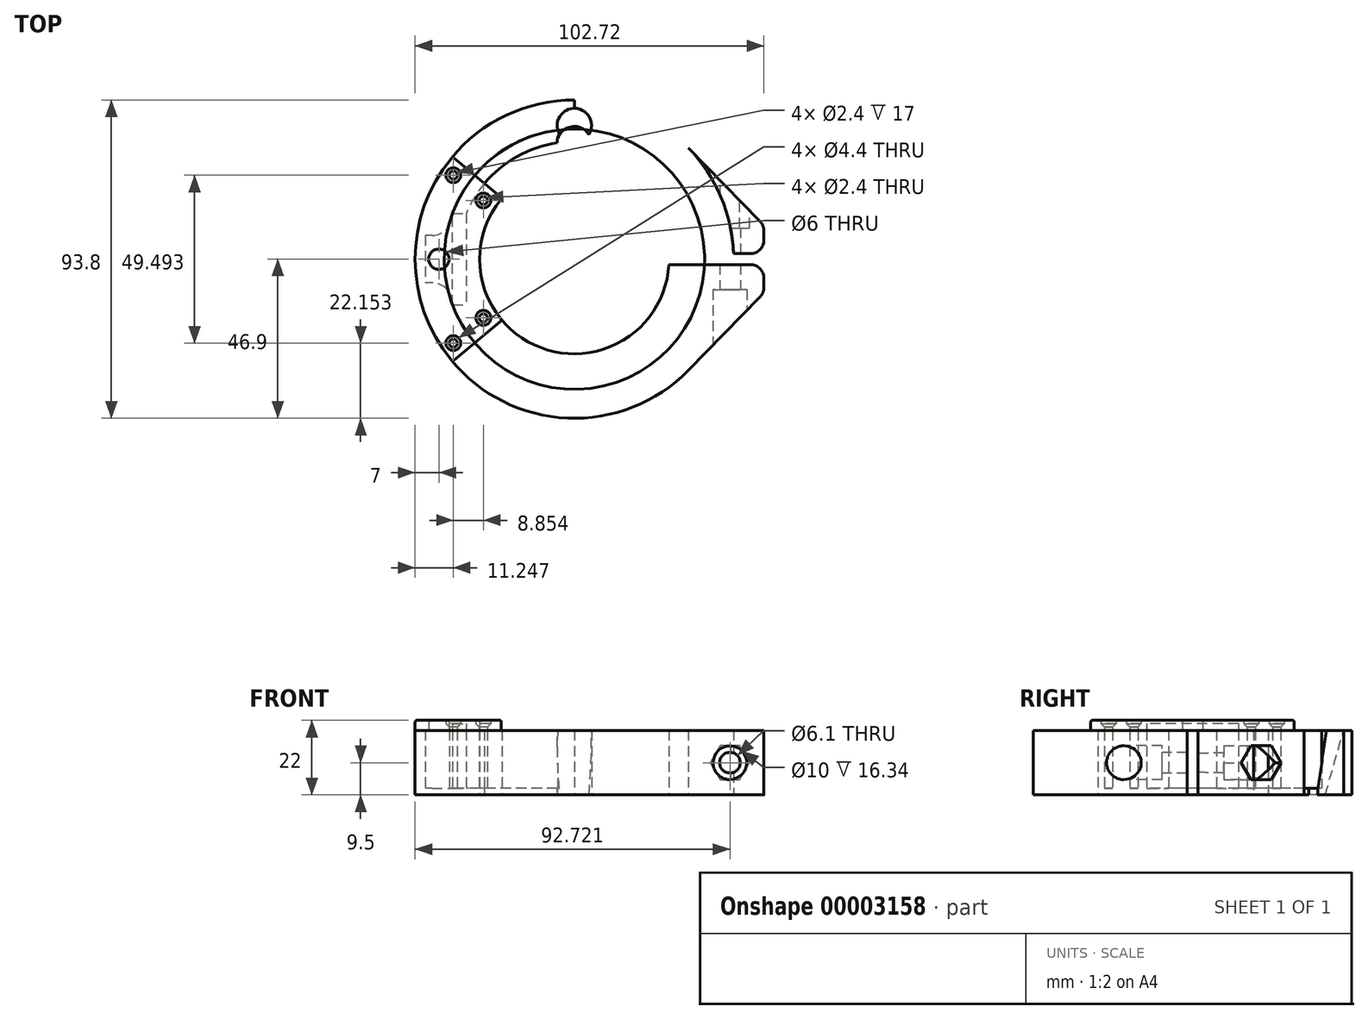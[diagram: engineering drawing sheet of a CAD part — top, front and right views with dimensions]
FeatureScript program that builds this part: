
annotation { "Feature Type Name" : "Feature", "Feature Type Description" : "" }
export const myFeature = defineFeature(function(context is Context, id is Id, definition is map)
    precondition{}
    {
        {
            var Q0;
            Q0=qCreatedBy(makeId("Top.planeOp"),FACE);
            var sketch = newSketch(context, id + "F0", { "sketchPlane" : qUnion([Q0])});
            skCircle(sketch, "E0", {"center": v(0, 0) * mm, "radius": 31.9 * mm, "construction": true});
            skCircle(sketch, "E1", {"center": v(0, 0) * mm, "radius": 43.4 * mm, "construction": true});
            skLineSegment(sketch, "E2", {"start": v(55.82, 1.6) * mm, "end": v(0, 1.6) * mm});
            skLineSegment(sketch, "E3", {"start": v(0, 1.6) * mm, "end": v(0, -1.6) * mm});
            skLineSegment(sketch, "E4", {"start": v(0, -1.6) * mm, "end": v(55.82, -1.6) * mm});
            skLineSegment(sketch, "E5", {"start": v(45.82, 10) * mm, "end": v(55.82, 10) * mm});
            skLineSegment(sketch, "E6", {"start": v(55.82, 10) * mm, "end": v(55.82, -10) * mm});
            skLineSegment(sketch, "E7", {"start": v(55.82, -10) * mm, "end": v(45.82, -10) * mm});
            skLineSegment(sketch, "E8", {"start": v(-31.9, 13.5) * mm, "end": v(-31.9, -13.5) * mm});
            skLineSegment(sketch, "E9", {"start": v(-35.9, -13.5) * mm, "end": v(-35.9, 13.5) * mm});
            skCircle(sketch, "E10", {"center": v(-39.9, 0) * mm, "radius": 3 * mm});
            skLineSegment(sketch, "E11", {"start": v(-35.9, 0) * mm, "end": v(-31.9, 0) * mm, "construction": true});
            skCircle(sketch, "E12", {"center": v(0, 0) * mm, "radius": 46.9 * mm});
            skLineSegment(sketch, "E13", {"start": v(-35.9, -13.5) * mm, "end": v(-31.9, -13.5) * mm});
            skLineSegment(sketch, "E14", {"start": v(-35.9, 13.5) * mm, "end": v(-31.9, 13.5) * mm});
            skLineSegment(sketch, "E15.rect.bottom", {"start": v(-35.9, 7) * mm, "end": v(-43.9, 7) * mm});
            skLineSegment(sketch, "E15.rect.top", {"start": v(-35.9, -7) * mm, "end": v(-43.9, -7) * mm});
            skLineSegment(sketch, "E15.rect.left", {"start": v(-35.9, 7) * mm, "end": v(-35.9, -7) * mm});
            skLineSegment(sketch, "E15.rect.right", {"start": v(-43.9, 7) * mm, "end": v(-43.9, -7) * mm});
            skCircle(sketch, "E16", {"center": v(0, 39.4) * mm, "radius": 5.05 * mm});
            skLineSegment(sketch, "E17", {"start": v(0, 31.9) * mm, "end": v(0, 46.9) * mm});
            skCircle(sketch, "E18", {"center": v(0, 0) * mm, "radius": 27.9 * mm});
            skLineSegment(sketch, "E19", {"start": v(-31.9, 0) * mm, "end": v(-27.9, 0) * mm});
            skLineSegment(sketch, "E20", {"start": v(0, 0) * mm, "end": v(55.82, 0) * mm, "construction": true});
            skArc(sketch, "E21", {"start": v(-4.87, 38.04) * mm, "mid": v(-23.8, 30.08) * mm, "end": v(-35.9, 13.5) * mm});
            skLineSegment(sketch, "E22", {"start": v(-21.36, 17.95) * mm, "end": v(-35.9, 30.18) * mm});
            skLineSegment(sketch, "E23", {"start": v(-35.9, -30.18) * mm, "end": v(-21.36, -17.95) * mm});
            skLineSegment(sketch, "E24", {"start": v(-35.9, 30.18) * mm, "end": v(-35.9, -30.18) * mm, "construction": true});
            skArc(sketch, "E25.trimOffspring", {"start": v(-1.6, 34.6) * mm, "mid": v(-19.8, 28.43) * mm, "end": v(-31.9, 13.5) * mm});
            skLineSegment(sketch, "E26.0", {"start": v(-38.34, -27) * mm, "end": v(-23.7, -14.7) * mm, "construction": true});
            skLineSegment(sketch, "E27.0", {"start": v(-23.7, 14.7) * mm, "end": v(-38.34, 27) * mm, "construction": true});
            skCircle(sketch, "E28", {"center": v(-26.8, 17.3) * mm, "radius": 1.2 * mm});
            skCircle(sketch, "E29", {"center": v(-35.65, 24.75) * mm, "radius": 1.2 * mm});
            skCircle(sketch, "E30", {"center": v(-35.65, -24.75) * mm, "radius": 1.2 * mm});
            skCircle(sketch, "E31", {"center": v(-26.8, -17.3) * mm, "radius": 1.2 * mm});
            skLineSegment(sketch, "E32", {"start": v(-43.9, 0) * mm, "end": v(-46.9, 0) * mm, "construction": true});
            skLineSegment(sketch, "E33", {"start": v(0, -43.4) * mm, "end": v(0, -46.9) * mm, "construction": true});
            skLineSegment(sketch, "E34", {"start": v(55.82, 10) * mm, "end": v(33.53, 32.8) * mm});
            skLineSegment(sketch, "E35", {"start": v(55.82, -10) * mm, "end": v(33.53, -32.8) * mm});
            skCircle(sketch, "E36.0", {"center": v(-35.65, 24.75) * mm, "radius": 2.2 * mm});
            skCircle(sketch, "E37.0", {"center": v(-26.8, 17.3) * mm, "radius": 2.2 * mm});
            skCircle(sketch, "E38.0", {"center": v(-35.65, -24.75) * mm, "radius": 2.2 * mm});
            skCircle(sketch, "E39.0", {"center": v(-26.8, -17.3) * mm, "radius": 2.2 * mm});
            skSolve(sketch);
        }
        {
            var Q0;
            {var subQ13=sQuery(id+"F0.wireOp",EDGE,"E13");Q0=makeQuery(id+"F0.imprint","IMPRINT",FACE,{"disambiguationData":[TD([[makeQuery(id+"F0.imprint","IMPRINT",EDGE,{"derivedFrom":subQ13}),-1.0]])]});}
            var Q1;
            {var subQ7=sQuery(id+"F0.wireOp",EDGE,"E19");Q1=makeQuery(id+"F0.imprint","IMPRINT",FACE,{"disambiguationData":[TD([[makeQuery(id+"F0.imprint","IMPRINT",EDGE,{"derivedFrom":subQ7}),1.0]])]});}
            var Q2;
            {var subQ3=sQuery(id+"F0.wireOp",EDGE,"E14");Q2=makeQuery(id+"F0.imprint","IMPRINT",FACE,{"disambiguationData":[TD([[makeQuery(id+"F0.imprint","IMPRINT",EDGE,{"derivedFrom":subQ3}),1.0]])]});}
            var Q3;
            {var subQ2=sQuery(id+"F0.wireOp",EDGE,"E13");Q3=makeQuery(id+"F0.imprint","IMPRINT",FACE,{"disambiguationData":[TD([[makeQuery(id+"F0.imprint","IMPRINT",EDGE,{"derivedFrom":subQ2}),1.0]])]});}
            var Q4;
            Q4=makeQuery(id+"F0.imprint","IMPRINT",FACE,{"disambiguationData":[TD([[makeQuery(id+"F0.imprint","IMPRINT",EDGE,{"derivedFrom":sQuery(id+"F0.wireOp",EDGE,"E10")}),-1.0]])]});
            extrude(context, id + "F1", {"entities" : qUnion([Q0, Q1, Q2, Q3, Q4]), "depth" : 3 * mm});
        }
        {
            var Q0;
            Q0=makeQuery(id+"F0.imprint","IMPRINT",FACE,{"disambiguationData":[TD([[makeQuery(id+"F0.imprint","IMPRINT",EDGE,{"derivedFrom":sQuery(id+"F0.wireOp",EDGE,"E28")}),-1.0]])]});
            var Q1;
            Q1=makeQuery(id+"F0.imprint","IMPRINT",FACE,{"disambiguationData":[TD([[makeQuery(id+"F0.imprint","IMPRINT",EDGE,{"derivedFrom":sQuery(id+"F0.wireOp",EDGE,"E29")}),-1.0]])]});
            var Q2;
            Q2=makeQuery(id+"F0.imprint","IMPRINT",FACE,{"disambiguationData":[TD([[makeQuery(id+"F0.imprint","IMPRINT",EDGE,{"derivedFrom":sQuery(id+"F0.wireOp",EDGE,"E30")}),-1.0]])]});
            var Q3;
            Q3=makeQuery(id+"F0.imprint","IMPRINT",FACE,{"disambiguationData":[TD([[makeQuery(id+"F0.imprint","IMPRINT",EDGE,{"derivedFrom":sQuery(id+"F0.wireOp",EDGE,"E31")}),-1.0]])]});
            extrude(context, id + "F2", {"entities" : qUnion([Q0, Q1, Q2, Q3]), "operationType" : NewBodyOperationType.ADD, "depth" : 2 * mm});
        }
        {
            var Q0;
            {var subQ2=sQuery(id+"F0.wireOp",EDGE,"E13");Q0=makeQuery(id+"F0.imprint","IMPRINT",FACE,{"disambiguationData":[TD([[makeQuery(id+"F0.imprint","IMPRINT",EDGE,{"derivedFrom":subQ2}),1.0]])]});}
            extrude(context, id + "F3", {"entities" : qUnion([Q0]), "operationType" : NewBodyOperationType.REMOVE, "depth" : 2 * mm});
        }
        {
            var Q0;
            Q0=makeQuery(id+"F1.opExtrude","SWEPT_BODY",BODY,{"disambiguationData":[OSD([sQuery(id+"F0.wireOp",EDGE,"E10"),sQuery(id+"F0.wireOp",EDGE,"E12"),sQuery(id+"F0.wireOp",EDGE,"E18"),sQuery(id+"F0.wireOp",EDGE,"E22"),sQuery(id+"F0.wireOp",EDGE,"E23"),sQuery(id+"F0.wireOp",EDGE,"E36.0"),sQuery(id+"F0.wireOp",EDGE,"E37.0"),sQuery(id+"F0.wireOp",EDGE,"E38.0"),sQuery(id+"F0.wireOp",EDGE,"E39.0")])]});
            transform(context, id + "F4", {"entities" : qUnion([Q0]), "transformType" : TransformType.TRANSLATION_3D, "dx" : 0 * mm, "dy" : 0 * mm, "dz" : 19 * mm, "makeCopy" : false});
        }
        {
            var Q0;
            Q0=makeQuery(id+"F2.opExtrude","CAP_EDGE",EDGE,{"disambiguationData":[OSD([sQuery(id+"F0.wireOp",EDGE,"E30")])],"isStart":false});
            var Q1;
            Q1=makeQuery(id+"F2.opExtrude","CAP_EDGE",EDGE,{"disambiguationData":[OSD([sQuery(id+"F0.wireOp",EDGE,"E31")])],"isStart":false});
            var Q2;
            Q2=makeQuery(id+"F2.opExtrude","CAP_EDGE",EDGE,{"disambiguationData":[OSD([sQuery(id+"F0.wireOp",EDGE,"E28")])],"isStart":false});
            var Q3;
            Q3=makeQuery(id+"F2.opExtrude","CAP_EDGE",EDGE,{"disambiguationData":[OSD([sQuery(id+"F0.wireOp",EDGE,"E29")])],"isStart":false});
            chamfer(context, id + "F5", {"entities" : qUnion([Q0, Q1, Q2, Q3]), "width" : 1 * mm, "tangentPropagation" : true});
        }
        {
            var Q0;
            Q0=makeQuery(id+"F1.opExtrude","CAP_EDGE",EDGE,{"disambiguationData":[OSD([sQuery(id+"F0.wireOp",EDGE,"E23")])],"isStart":false});
            var Q1;
            Q1=makeQuery(id+"F1.opExtrude","CAP_EDGE",EDGE,{"disambiguationData":[OSD([sQuery(id+"F0.wireOp",EDGE,"E22")])],"isStart":false});
            var Q2;
            Q2=makeQuery(id+"F1.opExtrude","CAP_EDGE",EDGE,{"disambiguationData":[OSD([sQuery(id+"F0.wireOp",EDGE,"E18")])],"isStart":false});
            var Q3;
            Q3=makeQuery(id+"F1.opExtrude","CAP_EDGE",EDGE,{"disambiguationData":[OSD([sQuery(id+"F0.wireOp",EDGE,"E12")])],"isStart":false});
            var Q4;
            Q4=makeQuery(id+"F1.opExtrude","SWEPT_EDGE",EDGE,{"disambiguationData":[OSD([sQuery(id+"F0.wireOp",EDGE,"E12"),sQuery(id+"F0.wireOp",EDGE,"E23")])]});
            var Q5;
            Q5=makeQuery(id+"F1.opExtrude","SWEPT_EDGE",EDGE,{"disambiguationData":[OSD([sQuery(id+"F0.wireOp",EDGE,"E18"),sQuery(id+"F0.wireOp",EDGE,"E23")])]});
            var Q6;
            Q6=makeQuery(id+"F1.opExtrude","SWEPT_EDGE",EDGE,{"disambiguationData":[OSD([sQuery(id+"F0.wireOp",EDGE,"E12"),sQuery(id+"F0.wireOp",EDGE,"E22")])]});
            var Q7;
            Q7=makeQuery(id+"F1.opExtrude","SWEPT_EDGE",EDGE,{"disambiguationData":[OSD([sQuery(id+"F0.wireOp",EDGE,"E18"),sQuery(id+"F0.wireOp",EDGE,"E22")])]});
            fillet(context, id + "F6", {"entities" : qUnion([Q0, Q1, Q2, Q3, Q4, Q5, Q6, Q7]), "radius" : .5 * mm, "tangentPropagation" : true, "allowEdgeOverflow" : false});
        }
        {
            var Q0;
            {var subQ13=sQuery(id+"F0.wireOp",EDGE,"E13");Q0=makeQuery(id+"F0.imprint","IMPRINT",FACE,{"disambiguationData":[TD([[makeQuery(id+"F0.imprint","IMPRINT",EDGE,{"derivedFrom":subQ13}),-1.0]])]});}
            var Q1;
            {var subQ3=sQuery(id+"F0.wireOp",EDGE,"E5");Q1=makeQuery(id+"F0.imprint","IMPRINT",FACE,{"disambiguationData":[TD([[makeQuery(id+"F0.imprint","IMPRINT",EDGE,{"derivedFrom":subQ3}),-1.0]])]});}
            var Q2;
            {var subQ3=sQuery(id+"F0.wireOp",EDGE,"E7");Q2=makeQuery(id+"F0.imprint","IMPRINT",FACE,{"disambiguationData":[TD([[makeQuery(id+"F0.imprint","IMPRINT",EDGE,{"derivedFrom":subQ3}),-1.0]])]});}
            var Q3;
            {var subQ0=sQuery(id+"F0.wireOp",EDGE,"E23");Q3=makeQuery(id+"F0.imprint","IMPRINT",FACE,{"disambiguationData":[TD([[makeQuery(id+"F0.imprint","IMPRINT",EDGE,{"derivedFrom":subQ0}),-1.0]])]});}
            var Q4;
            {var subQ3=sQuery(id+"F0.wireOp",EDGE,"E12");var subQ7=sQuery(id+"F0.wireOp",EDGE,"E17");var subQ9=makeQuery(id+"F0.imprint","INTERSECT",VERTEX,{"derivedFrom":[subQ3,subQ7]});Q4=makeQuery(id+"F0.imprint","IMPRINT",FACE,{"disambiguationData":[TD([[makeQuery(id+"F0.imprint","IMPRINT",EDGE,{"disambiguationData":[TD([[subQ9,-1.0]])],"derivedFrom":subQ3}),1.0]])]});}
            var Q5;
            {var subQ7=sQuery(id+"F0.wireOp",EDGE,"E19");Q5=makeQuery(id+"F0.imprint","IMPRINT",FACE,{"disambiguationData":[TD([[makeQuery(id+"F0.imprint","IMPRINT",EDGE,{"derivedFrom":subQ7}),1.0]])]});}
            var Q6;
            {var subQ9=sQuery(id+"F0.wireOp",EDGE,"E17");Q6=makeQuery(id+"F0.imprint","IMPRINT",FACE,{"disambiguationData":[TD([[makeQuery(id+"F0.imprint","IMPRINT",EDGE,{"disambiguationData":[TD([[makeQuery(id+"F0.imprint","IMPRINT",VERTEX,{"derivedFrom":sQuery(id+"F0.wireOp",VERTEX,"E17.start")}),-1.0]])],"derivedFrom":subQ9}),1.0]])]});}
            var Q7;
            {var subQ0=sQuery(id+"F0.wireOp",EDGE,"E17");var subQ1=sQuery(id+"F0.wireOp",EDGE,"E16");var subQ3=makeQuery(id+"F0.imprint","INTERSECT",VERTEX,{"disambiguationData":[OD(0.0)],"derivedFrom":[subQ1,subQ0]});Q7=makeQuery(id+"F0.imprint","IMPRINT",FACE,{"disambiguationData":[TD([[makeQuery(id+"F0.imprint","IMPRINT",EDGE,{"disambiguationData":[TD([[subQ3,-1.0]])],"derivedFrom":subQ1}),1.0]])]});}
            var Q8;
            {var subQ1=sQuery(id+"F0.wireOp",EDGE,"E16");var subQ5=makeQuery(id+"F0.imprint","INTERSECT",VERTEX,{"derivedFrom":[subQ1,sQuery(id+"F0.wireOp",EDGE,"E21")]});Q8=makeQuery(id+"F0.imprint","IMPRINT",FACE,{"disambiguationData":[TD([[makeQuery(id+"F0.imprint","IMPRINT",EDGE,{"disambiguationData":[TD([[subQ5,1.0]])],"derivedFrom":subQ1}),1.0]])]});}
            var Q9;
            Q9=makeQuery(id+"F0.imprint","IMPRINT",FACE,{"disambiguationData":[TD([[makeQuery(id+"F0.imprint","IMPRINT",EDGE,{"derivedFrom":sQuery(id+"F0.wireOp",EDGE,"E30")}),-1.0]])]});
            var Q10;
            Q10=makeQuery(id+"F0.imprint","IMPRINT",FACE,{"disambiguationData":[TD([[makeQuery(id+"F0.imprint","IMPRINT",EDGE,{"derivedFrom":sQuery(id+"F0.wireOp",EDGE,"E31")}),-1.0]])]});
            var Q11;
            Q11=makeQuery(id+"F0.imprint","IMPRINT",FACE,{"disambiguationData":[TD([[makeQuery(id+"F0.imprint","IMPRINT",EDGE,{"derivedFrom":sQuery(id+"F0.wireOp",EDGE,"E29")}),-1.0]])]});
            var Q12;
            Q12=makeQuery(id+"F0.imprint","IMPRINT",FACE,{"disambiguationData":[TD([[makeQuery(id+"F0.imprint","IMPRINT",EDGE,{"derivedFrom":sQuery(id+"F0.wireOp",EDGE,"E28")}),-1.0]])]});
            extrude(context, id + "F7", {"entities" : qUnion([Q0, Q1, Q2, Q3, Q4, Q5, Q6, Q7, Q8, Q9, Q10, Q11, Q12]), "depth" : 19 * mm});
        }
        {
            var Q0;
            {var subQ2=sQuery(id+"F0.wireOp",EDGE,"E13");Q0=makeQuery(id+"F0.imprint","IMPRINT",FACE,{"disambiguationData":[TD([[makeQuery(id+"F0.imprint","IMPRINT",EDGE,{"derivedFrom":subQ2}),1.0]])]});}
            var Q1;
            {var subQ3=sQuery(id+"F0.wireOp",EDGE,"E14");Q1=makeQuery(id+"F0.imprint","IMPRINT",FACE,{"disambiguationData":[TD([[makeQuery(id+"F0.imprint","IMPRINT",EDGE,{"derivedFrom":subQ3}),1.0]])]});}
            var Q2;
            {var subQ3=sQuery(id+"F0.wireOp",EDGE,"E16");var subQ5=sQuery(id+"F0.wireOp",EDGE,"E21");var subQ7=makeQuery(id+"F0.imprint","INTERSECT",VERTEX,{"derivedFrom":[subQ3,subQ5]});Q2=makeQuery(id+"F0.imprint","IMPRINT",FACE,{"disambiguationData":[TD([[makeQuery(id+"F0.imprint","IMPRINT",EDGE,{"disambiguationData":[TD([[subQ7,-1.0]])],"derivedFrom":subQ3}),-1.0]])]});}
            var Q3;
            Q3=makeQuery(id+"F0.imprint","IMPRINT",FACE,{"disambiguationData":[TD([[makeQuery(id+"F0.imprint","IMPRINT",EDGE,{"derivedFrom":sQuery(id+"F0.wireOp",EDGE,"E10")}),-1.0]])]});
            var Q4;
            Q4=makeQuery(id+"F0.imprint","IMPRINT",FACE,{"disambiguationData":[TD([[makeQuery(id+"F0.imprint","IMPRINT",EDGE,{"derivedFrom":sQuery(id+"F0.wireOp",EDGE,"E10")}),1.0]])]});
            extrude(context, id + "F8", {"entities" : qUnion([Q0, Q1, Q2, Q3, Q4]), "operationType" : NewBodyOperationType.ADD, "depth" : 2 * mm});
        }
        {
            var Q0;
            {var subQ2=sQuery(id+"F0.wireOp",EDGE,"E13");Q0=makeQuery(id+"F0.imprint","IMPRINT",FACE,{"disambiguationData":[TD([[makeQuery(id+"F0.imprint","IMPRINT",EDGE,{"derivedFrom":subQ2}),1.0]])]});}
            extrude(context, id + "F9", {"entities" : qUnion([Q0]), "operationType" : NewBodyOperationType.ADD, "depth" : 1 * mm});
        }
        {
            var Q0;
            Q0=makeQuery(id+"F0.imprint","IMPRINT",FACE,{"disambiguationData":[TD([[makeQuery(id+"F0.imprint","IMPRINT",EDGE,{"derivedFrom":sQuery(id+"F0.wireOp",EDGE,"E31")}),1.0]])]});
            var Q1;
            Q1=makeQuery(id+"F0.imprint","IMPRINT",FACE,{"disambiguationData":[TD([[makeQuery(id+"F0.imprint","IMPRINT",EDGE,{"derivedFrom":sQuery(id+"F0.wireOp",EDGE,"E30")}),1.0]])]});
            var Q2;
            Q2=makeQuery(id+"F0.imprint","IMPRINT",FACE,{"disambiguationData":[TD([[makeQuery(id+"F0.imprint","IMPRINT",EDGE,{"derivedFrom":sQuery(id+"F0.wireOp",EDGE,"E28")}),1.0]])]});
            var Q3;
            Q3=makeQuery(id+"F0.imprint","IMPRINT",FACE,{"disambiguationData":[TD([[makeQuery(id+"F0.imprint","IMPRINT",EDGE,{"derivedFrom":sQuery(id+"F0.wireOp",EDGE,"E29")}),1.0]])]});
            extrude(context, id + "F10", {"entities" : qUnion([Q0, Q1, Q2, Q3]), "operationType" : NewBodyOperationType.ADD, "depth" : 2 * mm});
        }
        {
            var Q0;
            Q0=makeQuery(id+"F7.opExtrude","SWEPT_EDGE",EDGE,{"disambiguationData":[OSD([sQuery(id+"F0.wireOp",EDGE,"E9"),sQuery(id+"F0.wireOp",EDGE,"E15.rect.bottom"),sQuery(id+"F0.wireOp",EDGE,"E15.rect.left")])]});
            var Q1;
            Q1=makeQuery(id+"F7.opExtrude","SWEPT_EDGE",EDGE,{"disambiguationData":[OSD([sQuery(id+"F0.wireOp",EDGE,"E9"),sQuery(id+"F0.wireOp",EDGE,"E15.rect.top"),sQuery(id+"F0.wireOp",EDGE,"E15.rect.left")])]});
            fillet(context, id + "F11", {"entities" : qUnion([Q0, Q1]), "radius" : 6 * mm, "tangentPropagation" : true, "allowEdgeOverflow" : false});
        }
        {
            var Q0;
            Q0=makeQuery(id+"F7.opExtrude","SWEPT_FACE",FACE,{"disambiguationData":[OSD([sQuery(id+"F0.wireOp",EDGE,"E7")])]});
            var sketch = newSketch(context, id + "F12", { "sketchPlane" : qUnion([Q0])});
            skCircle(sketch, "E40", {"center": v(45.82, 9.5) * mm, "radius": 3.05 * mm});
            skSolve(sketch);
        }
        {
            var Q0;
            {var subQ2=sQuery(id+"F0.wireOp",EDGE,"E7");Q0=makeQuery(id+"F0.imprint","IMPRINT",FACE,{"disambiguationData":[TD([[makeQuery(id+"F0.imprint","IMPRINT",EDGE,{"derivedFrom":subQ2}),1.0]])]});}
            var Q1;
            {var subQ2=sQuery(id+"F0.wireOp",EDGE,"E5");Q1=makeQuery(id+"F0.imprint","IMPRINT",FACE,{"disambiguationData":[TD([[makeQuery(id+"F0.imprint","IMPRINT",EDGE,{"derivedFrom":subQ2}),1.0]])]});}
            extrude(context, id + "F13", {"entities" : qUnion([Q0, Q1]), "operationType" : NewBodyOperationType.ADD, "depth" : 19 * mm});
        }
        {
            var Q0;
            {var subQ0=makeQuery(id+"F7.opExtrude","SWEPT_EDGE",EDGE,{"disambiguationData":[OSD([sQuery(id+"F0.wireOp",EDGE,"E7"),sQuery(id+"F0.wireOp",EDGE,"E12")])]});var subQ1=sQuery(id+"F12.wireOp",EDGE,"E40");var subQ3=makeQuery(id+"F12.imprint","INTERSECT",VERTEX,{"disambiguationData":[OD(0.0)],"derivedFrom":[subQ0,subQ1]});Q0=qUnion([makeQuery(id+"F12.imprint","IMPRINT",FACE,{"disambiguationData":[TD([[makeQuery(id+"F12.imprint","IMPRINT",EDGE,{"disambiguationData":[TD([[subQ3,1.0]])],"derivedFrom":subQ1}),1.0]])]}),makeQuery(id+"F12.imprint","IMPRINT",FACE,{"disambiguationData":[TD([[makeQuery(id+"F12.imprint","IMPRINT",EDGE,{"disambiguationData":[TD([[subQ3,-1.0]])],"derivedFrom":subQ1}),1.0]])]})]);}
            extrude(context, id + "F14", {"entities" : qUnion([Q0]), "operationType" : NewBodyOperationType.REMOVE, "endBound" : BoundingType.SYMMETRIC, "oppositeDirection" : true, "depth" : 100 * mm});
        }
        {
            var Q0;
            {var subQ0=sQuery(id+"F0.wireOp",EDGE,"E6");var subQ1=sQuery(id+"F0.wireOp",EDGE,"E7");var subQ2=sQuery(id+"F0.wireOp",EDGE,"E35");Q0=makeQuery(id+"F13.boolean.opBoolean","MERGE",EDGE,{"derivedFrom":[makeQuery(id+"F7.opExtrude","SWEPT_EDGE",EDGE,{"disambiguationData":[OSD([subQ0,subQ1,subQ2])]}),makeQuery(id+"F13.opExtrude","SWEPT_EDGE",EDGE,{"disambiguationData":[OSD([subQ0,subQ1,subQ2])]})]});}
            var Q1;
            {var subQ0=sQuery(id+"F0.wireOp",EDGE,"E5");var subQ1=sQuery(id+"F0.wireOp",EDGE,"E6");var subQ2=sQuery(id+"F0.wireOp",EDGE,"E34");Q1=makeQuery(id+"F13.boolean.opBoolean","MERGE",EDGE,{"derivedFrom":[makeQuery(id+"F7.opExtrude","SWEPT_EDGE",EDGE,{"disambiguationData":[OSD([subQ0,subQ1,subQ2])]}),makeQuery(id+"F13.opExtrude","SWEPT_EDGE",EDGE,{"disambiguationData":[OSD([subQ0,subQ1,subQ2])]})]});}
            var Q2;
            Q2=makeQuery(id+"F7.opExtrude","SWEPT_EDGE",EDGE,{"disambiguationData":[OSD([sQuery(id+"F0.wireOp",EDGE,"E2"),sQuery(id+"F0.wireOp",EDGE,"E6")])]});
            var Q3;
            Q3=makeQuery(id+"F7.opExtrude","SWEPT_EDGE",EDGE,{"disambiguationData":[OSD([sQuery(id+"F0.wireOp",EDGE,"E4"),sQuery(id+"F0.wireOp",EDGE,"E6")])]});
            fillet(context, id + "F15", {"entities" : qUnion([Q0, Q1, Q2, Q3]), "radius" : 4 * mm, "tangentPropagation" : true, "allowEdgeOverflow" : false});
        }
        {
            var Q0;
            Q0=qCreatedBy(makeId("Front.planeOp"),FACE);
            cPlane(context, id + "F16", {"entities" : qUnion([Q0]), "cplaneType" : CPlaneType.OFFSET, "offset" : 27 * mm, "oppositeDirection" : true, "width" : 150 * mm, "height" : 150 * mm});
        }
        {
            var Q0;
            Q0=qCreatedBy(id+"F16.planeOp",FACE);
            var sketch = newSketch(context, id + "F17", { "sketchPlane" : qUnion([Q0])});
            skCircle(sketch, "E41.1", {"center": v(45.82, 9.5) * mm, "radius": 3.05 * mm});
            skCircle(sketch, "E42.cCircle", {"center": v(45.82, 9.5) * mm, "radius": 5 * mm, "construction": true});
            skLineSegment(sketch, "E42.0", {"start": v(48.7, 14.5) * mm, "end": v(51.6, 9.5) * mm});
            skLineSegment(sketch, "E42.1", {"start": v(51.6, 9.5) * mm, "end": v(48.7, 4.5) * mm});
            skLineSegment(sketch, "E42.2", {"start": v(48.7, 4.5) * mm, "end": v(42.93, 4.5) * mm});
            skLineSegment(sketch, "E42.3", {"start": v(42.93, 4.5) * mm, "end": v(40.05, 9.5) * mm});
            skLineSegment(sketch, "E42.4", {"start": v(40.05, 9.5) * mm, "end": v(42.93, 14.5) * mm});
            skLineSegment(sketch, "E42.5", {"start": v(42.93, 14.5) * mm, "end": v(48.7, 14.5) * mm});
            skPoint(sketch, "E42.0.midPoint", {"position": v(50.15, 12) * mm});
            skSolve(sketch);
        }
        {
            var Q0;
            Q0=makeQuery(id+"F17.imprint","IMPRINT",FACE,{"disambiguationData":[TD([[makeQuery(id+"F17.imprint","IMPRINT",EDGE,{"derivedFrom":sQuery(id+"F17.wireOp",EDGE,"E41.1")}),-1.0]])]});
            extrude(context, id + "F18", {"entities" : qUnion([Q0]), "operationType" : NewBodyOperationType.REMOVE, "depth" : 17.8 * mm});
        }
        {
            var Q0;
            Q0=qCreatedBy(makeId("Front.planeOp"),FACE);
            cPlane(context, id + "F19", {"entities" : qUnion([Q0]), "cplaneType" : CPlaneType.OFFSET, "offset" : 27 * mm, "width" : 150 * mm, "height" : 150 * mm});
        }
        {
            var Q0;
            Q0=qCreatedBy(id+"F19.planeOp",FACE);
            var sketch = newSketch(context, id + "F20", { "sketchPlane" : qUnion([Q0])});
            skCircle(sketch, "E43.0", {"center": v(45.82, 9.5) * mm, "radius": 3.05 * mm});
            skCircle(sketch, "E44", {"center": v(45.82, 9.5) * mm, "radius": 5 * mm});
            skSolve(sketch);
        }
        {
            var Q0;
            Q0=makeQuery(id+"F20.imprint","IMPRINT",FACE,{"disambiguationData":[TD([[makeQuery(id+"F20.imprint","IMPRINT",EDGE,{"derivedFrom":sQuery(id+"F20.wireOp",EDGE,"E43.0")}),-1.0]])]});
            extrude(context, id + "F21", {"entities" : qUnion([Q0]), "operationType" : NewBodyOperationType.REMOVE, "oppositeDirection" : true, "depth" : 18 * mm});
        }
        {
            var Q0;
            Q0=qCreatedBy(makeId("Right.planeOp"),FACE);
            var sketch = newSketch(context, id + "F22", { "sketchPlane" : qUnion([Q0])});
            skLineSegment(sketch, "E45", {"start": v(0, 0) * mm, "end": v(0, -121) * mm});
            skLineSegment(sketch, "E46", {"start": v(0, -121) * mm, "end": v(75.18, 146.15) * mm});
            skSolve(sketch);
        }
        {
            var Q0;
            Q0=qCreatedBy(makeId("Top.planeOp"),FACE);
            cPlane(context, id + "F23", {"entities" : qUnion([Q0]), "cplaneType" : CPlaneType.OFFSET, "offset" : 121 * mm, "oppositeDirection" : true, "width" : 150 * mm, "height" : 150 * mm});
        }
        {
            var Q0;
            Q0=qCreatedBy(id+"F23.planeOp",FACE);
            var sketch = newSketch(context, id + "F24", { "sketchPlane" : qUnion([Q0])});
            skCircle(sketch, "E47", {"center": v(0, 0) * mm, "radius": 5.05 * mm});
            skCircle(sketch, "E48.0", {"center": v(0, 39.4) * mm, "radius": 5.05 * mm});
            skSolve(sketch);
        }
        {
            var Q0;
            Q0=makeQuery(id+"F24.imprint","IMPRINT",FACE,{"disambiguationData":[TD([[makeQuery(id+"F24.imprint","IMPRINT",EDGE,{"derivedFrom":sQuery(id+"F24.wireOp",EDGE,"E47")}),1.0]])]});
            var Q1;
            Q1=sQuery(id+"F22.wireOp",EDGE,"E46");
            sweep(context, id + "F25", {"operationType" : NewBodyOperationType.REMOVE, "profiles" : qUnion([Q0]), "path" : qUnion([Q1])});
        }
    });
